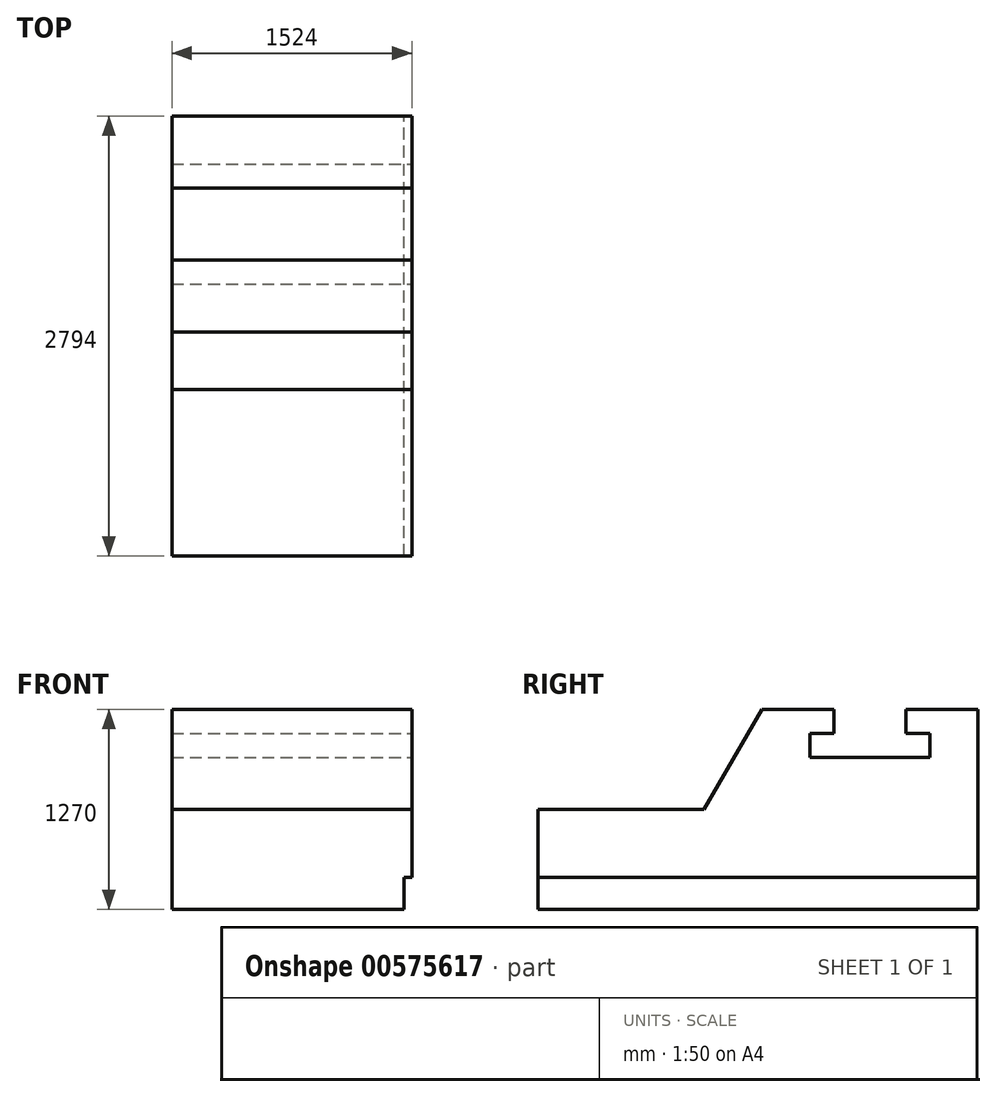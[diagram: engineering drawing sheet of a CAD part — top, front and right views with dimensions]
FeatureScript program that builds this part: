
annotation { "Feature Type Name" : "Feature", "Feature Type Description" : "" }
export const myFeature = defineFeature(function(context is Context, id is Id, definition is map)
    precondition{}
    {
        {
            var Q0;
            Q0=qCreatedBy(makeId("Right.planeOp"),FACE);
            var sketch = newSketch(context, id + "F0", { "sketchPlane" : qUnion([Q0])});
            skLineSegment(sketch, "E0.bottom", {"start": v(0, 0) * mm, "end": v(2794, 0) * mm});
            skLineSegment(sketch, "E0.top", {"start": v(0, -635) * mm, "end": v(2794, -635) * mm});
            skLineSegment(sketch, "E0.left", {"start": v(0, 0) * mm, "end": v(0, -635) * mm});
            skLineSegment(sketch, "E0.right", {"start": v(2794, 0) * mm, "end": v(2794, -635) * mm});
            skSolve(sketch);
        }
        {
            var Q0;
            Q0=makeQuery(id+"F0.imprint","IMPRINT",FACE,{"disambiguationData":[TD([[makeQuery(id+"F0.imprint","IMPRINT",EDGE,{"derivedFrom":sQuery(id+"F0.wireOp",EDGE,"E0.bottom")}),-1.0]])]});
            extrude(context, id + "F1", {"entities" : qUnion([Q0]), "oppositeDirection" : true, "depth" : 1524 * mm, "offsetDistance" : 25.4 * mm});
        }
        {
            var Q0;
            Q0=makeQuery(id+"F1.opExtrude","CAP_FACE",FACE,{"disambiguationData":[OSD([sQuery(id+"F0.wireOp",EDGE,"E0.bottom"),sQuery(id+"F0.wireOp",EDGE,"E0.top"),sQuery(id+"F0.wireOp",EDGE,"E0.left"),sQuery(id+"F0.wireOp",EDGE,"E0.right")])],"isStart":true});
            var sketch = newSketch(context, id + "F2", { "sketchPlane" : qUnion([Q0])});
            skLineSegment(sketch, "E1", {"start": v(2794, 0) * mm, "end": v(2794, 635) * mm});
            skLineSegment(sketch, "E2", {"start": v(2794, 635) * mm, "end": v(2336.8, 635) * mm});
            skLineSegment(sketch, "E3", {"start": v(2336.8, 635) * mm, "end": v(2336.8, 482.6) * mm});
            skLineSegment(sketch, "E4", {"start": v(2336.8, 482.6) * mm, "end": v(2489.2, 482.6) * mm});
            skLineSegment(sketch, "E5", {"start": v(2489.2, 482.6) * mm, "end": v(2489.2, 330.2) * mm});
            skLineSegment(sketch, "E6", {"start": v(2489.2, 330.2) * mm, "end": v(1727.2, 330.2) * mm});
            skLineSegment(sketch, "E7", {"start": v(1727.2, 330.2) * mm, "end": v(1727.2, 482.6) * mm});
            skLineSegment(sketch, "E8", {"start": v(1727.2, 482.6) * mm, "end": v(1879.6, 482.6) * mm});
            skLineSegment(sketch, "E9", {"start": v(1879.6, 482.6) * mm, "end": v(1879.6, 635) * mm});
            skLineSegment(sketch, "E10", {"start": v(1879.6, 635) * mm, "end": v(1422.4, 635) * mm});
            skLineSegment(sketch, "E11", {"start": v(1422.4, 635) * mm, "end": v(1055.78, 0) * mm});
            skSolve(sketch);
        }
        {
            var Q0;
            {var subQ0=sQuery(id+"F2.wireOp",EDGE,"E1");Q0=makeQuery(id+"F2.imprint","IMPRINT",FACE,{"disambiguationData":[TD([[makeQuery(id+"F2.imprint","IMPRINT",EDGE,{"derivedFrom":subQ0}),1.0]])]});}
            extrude(context, id + "F3", {"entities" : qUnion([Q0]), "operationType" : NewBodyOperationType.ADD, "oppositeDirection" : true, "depth" : 1524 * mm, "offsetDistance" : 25.4 * mm});
        }
        {
            var Q0;
            {var subQ0=sQuery(id+"F0.wireOp",EDGE,"E0.bottom");Q0=makeQuery(id+"F3.boolean.opBoolean","MERGE",FACE,{"derivedFrom":[makeQuery(id+"F1.opExtrude","CAP_FACE",FACE,{"disambiguationData":[OSD([subQ0,sQuery(id+"F0.wireOp",EDGE,"E0.top"),sQuery(id+"F0.wireOp",EDGE,"E0.left"),sQuery(id+"F0.wireOp",EDGE,"E0.right")])],"isStart":true}),makeQuery(id+"F3.opExtrude","CAP_FACE",FACE,{"disambiguationData":[OSD([subQ0,sQuery(id+"F2.wireOp",EDGE,"E1"),sQuery(id+"F2.wireOp",EDGE,"E2"),sQuery(id+"F2.wireOp",EDGE,"E3"),sQuery(id+"F2.wireOp",EDGE,"E4"),sQuery(id+"F2.wireOp",EDGE,"E5"),sQuery(id+"F2.wireOp",EDGE,"E6"),sQuery(id+"F2.wireOp",EDGE,"E7"),sQuery(id+"F2.wireOp",EDGE,"E8"),sQuery(id+"F2.wireOp",EDGE,"E9"),sQuery(id+"F2.wireOp",EDGE,"E10"),sQuery(id+"F2.wireOp",EDGE,"E11")])],"isStart":true})]});}
            var sketch = newSketch(context, id + "F4", { "sketchPlane" : qUnion([Q0])});
            skLineSegment(sketch, "E12.bottom", {"start": v(0, -635) * mm, "end": v(2794, -635) * mm});
            skLineSegment(sketch, "E12.top", {"start": v(0, -431.8) * mm, "end": v(2794, -431.8) * mm});
            skLineSegment(sketch, "E12.left", {"start": v(0, -635) * mm, "end": v(0, -431.8) * mm});
            skLineSegment(sketch, "E12.right", {"start": v(2794, -635) * mm, "end": v(2794, -431.8) * mm});
            skSolve(sketch);
        }
        {
            var Q0;
            Q0=makeQuery(id+"F4.imprint","IMPRINT",FACE,{"disambiguationData":[TD([[makeQuery(id+"F4.imprint","IMPRINT",EDGE,{"derivedFrom":sQuery(id+"F4.wireOp",EDGE,"E12.bottom")}),1.0]])]});
            extrude(context, id + "F5", {"entities" : qUnion([Q0]), "operationType" : NewBodyOperationType.REMOVE, "oppositeDirection" : true, "depth" : 50.8 * mm, "offsetDistance" : 25.4 * mm});
        }
    });
